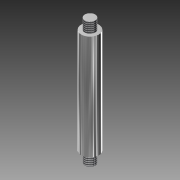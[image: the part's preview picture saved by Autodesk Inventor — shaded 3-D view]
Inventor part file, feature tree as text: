
AUTODESK INVENTOR PART (.ipt)
format: ipt  version: 2012 (Build 160160000, 160)  size: 83,968 bytes
history: native  units: mm
features: extrude x3, sketch x3, thread x2
ambient origin geometry x8: Origin, YZ Plane, XZ Plane, XY Plane, X Axis, Y Axis, Z Axis, Center Point
bodies: Solid1 (feature_tree)
feature tree (8):
  extrude  "Extrusion1"  Depth=30.0mm TaperAngle=0.0deg
  extrude  "Extrusion2"  Depth=3.0mm TaperAngle=0.0deg
  thread  "Thread1"  [1 undecoded]
  extrude  "Extrusion3"  Depth=3.0mm TaperAngle=0.0deg
  thread  "Thread2"  [1 undecoded]
  sketch  "Sketch1"  dims[d0=5.0mm d1=30.0mm d2=0.0mm]
  sketch  "Sketch2"  dims[d3=3.0mm d4=3.0mm d5=0.0mm d6=10.0mm d7=0.0mm]
  sketch  "Sketch3"  dims[d8=3.0mm d9=3.0mm d10=0.0mm d11=10.0mm d12=0.0mm]
note: 2 required parameter values undecoded (feature->parameter linkage not recoverable at this tier; creation-order binding heuristic only, values carry confidence <= 0.55)
